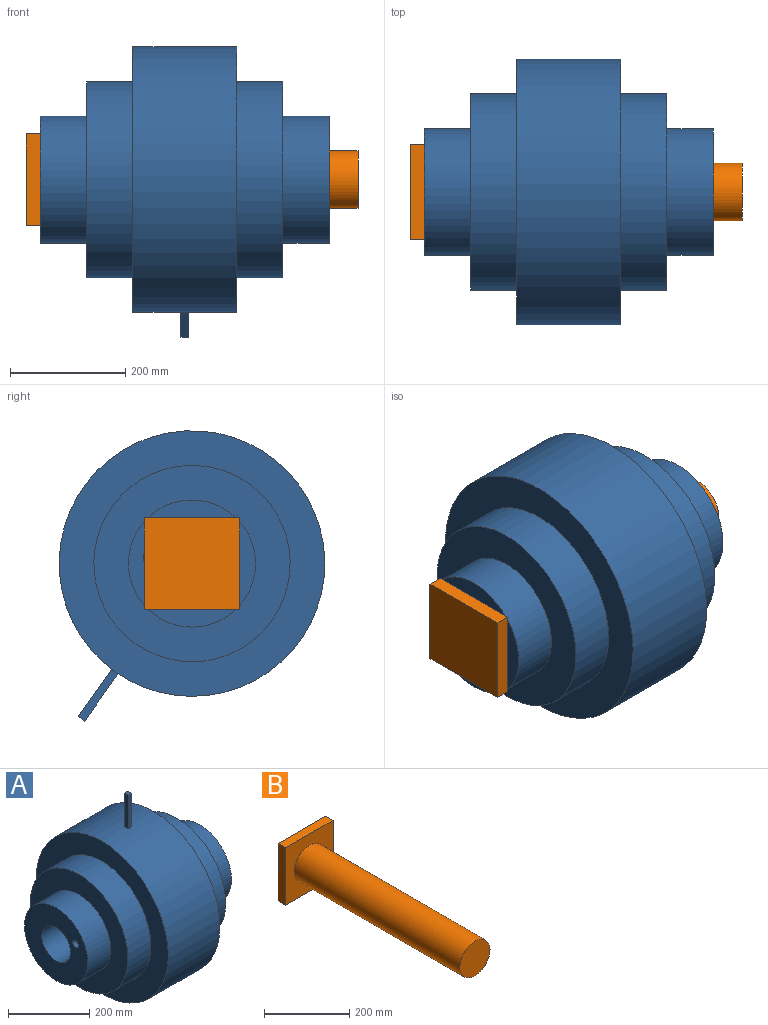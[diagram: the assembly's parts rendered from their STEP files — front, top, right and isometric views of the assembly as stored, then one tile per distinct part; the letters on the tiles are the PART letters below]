
ASSEMBLY  parts=2 mates=1
PART A: 18 faces, bbox 500x460x560 mm
  f0: cylinder r=230mm len=460mm, axis (-1,0,0), area 259936.1mm2, adj f1,f11,f13,f14,f15,f16
  f1: plane 460x460mm, normal (-1,0,0), area 75398.2mm2, adj f0,f2
  f2: cylinder r=170mm len=340mm, axis (-1,0,0), area 85451.3mm2, adj f1,f3
  f3: plane 340x340mm, normal (-1,0,0), area 52778.8mm2, adj f2,f4
  f4: cylinder r=110mm len=220mm, axis (-1,0,0), area 55292mm2, adj f3,f5
  f5: plane 220x220mm, normal (-1,0,0), area 29845.1mm2, adj f4,f6,f12
  f6: cylinder r=50mm len=500mm, axis (-1,0,0), area 157079.6mm2, adj f5,f7
  f7: plane 220x220mm, normal (1,0,0), area 29845.1mm2, adj f6,f8,f12
  f8: cylinder r=110mm len=220mm, axis (-1,0,0), area 55292mm2, adj f7,f9
  f9: plane 340x340mm, normal (1,0,0), area 52778.8mm2, adj f8,f10
  f10: cylinder r=170mm len=340mm, axis (-1,0,0), area 85451.3mm2, adj f9,f11
  f11: plane 460x460mm, normal (1,0,0), area 75398.2mm2, adj f0,f10
  f12: cylinder r=10mm len=500mm, axis (-1,0,0), area 31415.9mm2, adj f5,f7
  f13: plane 100.11x13.44mm, normal (0,-1,0), area 1345.1mm2, adj f0,f15,f16,f17
  f14: plane 100.11x13.44mm, normal (0,1,0), area 1345.1mm2, adj f0,f15,f16,f17
  f15: plane 100.11x13.97mm, normal (1,0,0), area 1398mm2, adj f0,f13,f14,f17
  f16: plane 100.11x13.97mm, normal (-1,0,0), area 1398mm2, adj f0,f13,f14,f17
  f17: plane 13.97x13.44mm, normal (0,0,1), area 187.8mm2, adj f13,f14,f15,f16
PART B: 8 faces, bbox 157.9x575x165.2 mm
  f0: cylinder r=50mm len=550mm, axis (0,1,0), area 172787.6mm2, adj f1,f7
  f1: plane 100x100mm, normal (0,-1,0), area 7854mm2, adj f0
  f2: plane 157.86x25mm, normal (0,0,-1), area 3946.5mm2, adj f3,f5,f6,f7
  f3: plane 165.23x25mm, normal (-1,0,0), area 4130.7mm2, adj f2,f4,f6,f7
  f4: plane 157.86x25mm, normal (0,0,1), area 3946.5mm2, adj f3,f5,f6,f7
  f5: plane 165.23x25mm, normal (1,0,0), area 4130.7mm2, adj f2,f4,f6,f7
  f6: plane 165.23x157.86mm, normal (0,1,0), area 26083mm2, adj f2,f3,f4,f5
  f7: plane 165.23x157.86mm, normal (0,-1,0), area 18229mm2, adj f0,f2,f3,f4,f5
PLACE A rot(axis=(-1,0,0),144.5deg) t=(35.24,-71.75,-375.54)mm
PLACE B rot(axis=(0.58,-0.58,0.58),120deg) t=(-214.76,-71.75,-375.54)mm fixed
MATE cylindrical B.f0 <-> A.f0  axis (1,0,0) through (-214.76,-71.75,-375.54)mm
